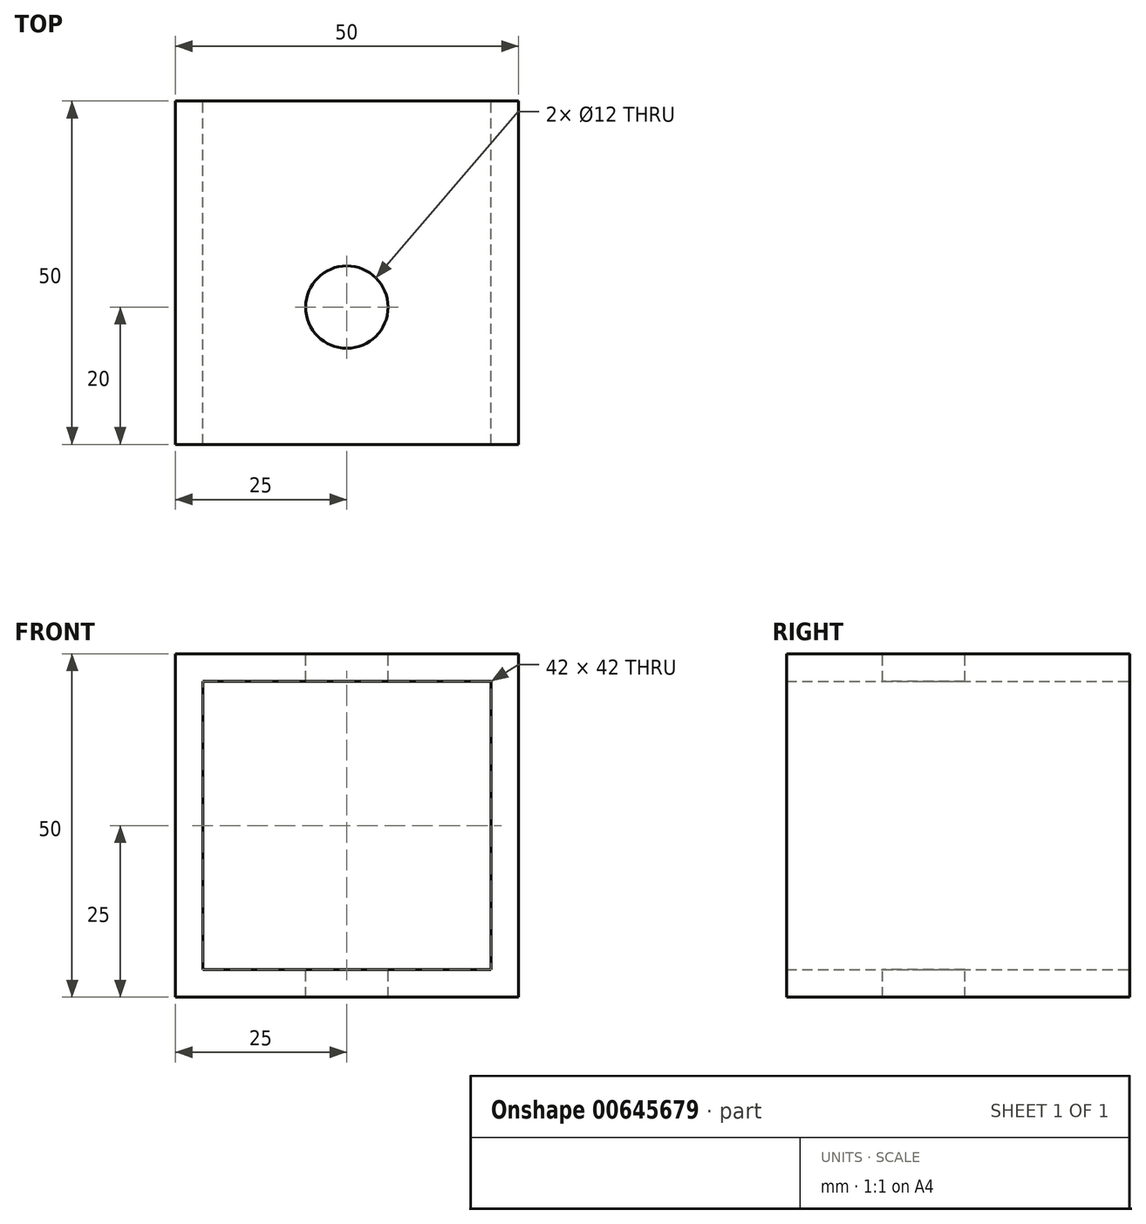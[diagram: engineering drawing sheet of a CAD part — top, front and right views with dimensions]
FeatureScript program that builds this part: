
annotation { "Feature Type Name" : "Feature", "Feature Type Description" : "" }
export const myFeature = defineFeature(function(context is Context, id is Id, definition is map)
    precondition{}
    {
        {
            var Q0;
            Q0=qCreatedBy(makeId("Front.planeOp"),FACE);
            var sketch = newSketch(context, id + "F0", { "sketchPlane" : qUnion([Q0])});
            skLineSegment(sketch, "E0.bottom", {"start": v(-50, 0) * mm, "end": v(0, 0) * mm});
            skLineSegment(sketch, "E0.top", {"start": v(-50, -50) * mm, "end": v(0, -50) * mm});
            skLineSegment(sketch, "E0.left", {"start": v(-50, 0) * mm, "end": v(-50, -50) * mm});
            skLineSegment(sketch, "E0.right", {"start": v(0, 0) * mm, "end": v(0, -50) * mm});
            skLineSegment(sketch, "E1.bottom", {"start": v(-46, -4) * mm, "end": v(-4, -4) * mm});
            skLineSegment(sketch, "E1.top", {"start": v(-46, -46) * mm, "end": v(-4, -46) * mm});
            skLineSegment(sketch, "E1.left", {"start": v(-46, -4) * mm, "end": v(-46, -46) * mm});
            skLineSegment(sketch, "E1.right", {"start": v(-4, -4) * mm, "end": v(-4, -46) * mm});
            skSolve(sketch);
        }
        {
            var Q0;
            Q0=makeQuery(id+"F0.imprint","IMPRINT",FACE,{"disambiguationData":[TD([[makeQuery(id+"F0.imprint","IMPRINT",EDGE,{"derivedFrom":sQuery(id+"F0.wireOp",EDGE,"E0.bottom")}),-1.0]])]});
            extrude(context, id + "F1", {"entities" : qUnion([Q0]), "depth" : 50 * mm, "offsetDistance" : 25 * mm});
        }
        {
            var Q0;
            Q0=makeQuery(id+"F1.opExtrude","SWEPT_FACE",FACE,{"disambiguationData":[OSD([sQuery(id+"F0.wireOp",EDGE,"E0.bottom")])]});
            var sketch = newSketch(context, id + "F2", { "sketchPlane" : qUnion([Q0])});
            skLineSegment(sketch, "E2", {"start": v(-25, -50) * mm, "end": v(-25, 0) * mm, "construction": true});
            skCircle(sketch, "E3", {"center": v(-25, -30) * mm, "radius": 6 * mm});
            skSolve(sketch);
        }
        {
            var Q0;
            Q0 = qSketchRegion(id + "F2", true);
            extrude(context, id + "F3", {"entities" : qUnion([Q0]), "operationType" : NewBodyOperationType.REMOVE, "endBound" : BoundingType.THROUGH_ALL, "oppositeDirection" : true, "depth" : 25 * mm, "offsetDistance" : 25 * mm});
        }
    });
